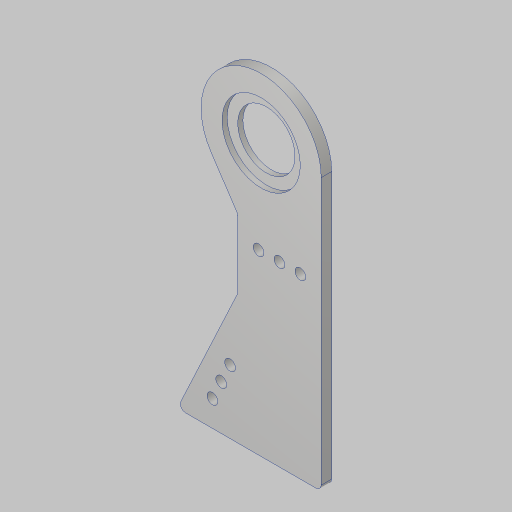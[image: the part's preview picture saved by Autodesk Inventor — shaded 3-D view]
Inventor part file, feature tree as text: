
AUTODESK INVENTOR PART (.ipt)
format: ipt  version: 2023.5 (Build 275446000, 446)  size: 173,568 bytes
history: native  units: in
note: dims shown in document units (in); Inventor stores cm internally (conversion verified against a paired STEP export)
features: sketch x3, extrude x2, projected_geometry x2, hole x1, fillet x1
ambient origin geometry x8: Origin, YZ Plane, XZ Plane, XY Plane, X Axis, Y Axis, Z Axis, Center Point
bodies: Solid1 (feature_tree)
feature tree (9):
  sketch  "Sketch1"  dims[d0=1.875in d1=0.5in]
  extrude  "Extrusion1"  Depth=0.5in
  hole  "Hole1"  [1 undecoded]
  extrude  "Extrusion2"  Depth=0.125in
  sketch  "Sketch3"  dims[d4=2.0in d5=15.25in d6=1.0in d7=0.1718in d8=15.0in d10=1.0in d11=2.75in d13=17.0in d15=7.375in d17=0.5in d18=0.5in d19=0.5in d20=0.5in d21=1.9685in d23=0.5in d24=0.3937in d26=1.0in d28=0.25in d29=0.0in d30=0.26in d31=0.75in d32=0.385in d33=0.25in d34=0.5635in d35=1.0in d36=0.8108in d37=0.25in d38=0.125in d39=0.0in d40=0.125in]
  fillet  "Fillet1"  Radius=1.0in
  sketch  "Sketch2"  dims[d2=2.0in d3=6.5in]
  projected_geometry  "Project Cut Edges1"
  projected_geometry  "Project Cut Edges2"
note: 1 required parameter value undecoded (feature->parameter linkage not recoverable at this tier; creation-order binding heuristic only, values carry confidence <= 0.55)
